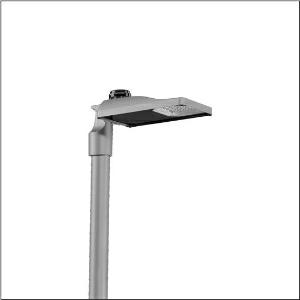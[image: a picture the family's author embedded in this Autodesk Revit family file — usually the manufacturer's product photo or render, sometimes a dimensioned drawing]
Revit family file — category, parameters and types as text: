
# Revit family: streetlight_sl_31_micro___p1_0a_5xh5a75n08da_cf7a
name_source: partatom
category: Lighting Fixtures
units: mm (PartAtom-declared; Revit-internal decimal feet)

## family parameters
Cut with Voids When Loaded = No
Host = Face
Light Source = No
Part Type = Normal
Room Calculation Point = No
Round Connector Dimension = Use Diameter
Shared = No

## types (1)
- --- (1 x LED, 3700 lm, 35.5 W, 2200K)
    Apparent Load = 36 VA
    CIE Flux Codes = 23 55 94 100 100
    Color Rendering = 70
    Color Temperature = 2200K
    Default Elevation = 1800 mm
    Description = Streetlight SL 31 micro NEMA (7pin), Desk-Remote mast luminaire for post-top, side-entry; light control with lens of PMMA; light distribution: P1.0a, direct asymmetric distribution, for standard-compliant lighting for roads and squares; LED: luminous flux: 3.700lm, light colour: 722, colour temperature: 2200K; luminous efficacy: 104,2lm/W; control: pre-setting: linear dimming characteristic, flexible luminous flux parameterisation, time-dependent luminous flux control, constant luminous flux control, intelligent temperature release in ECG and LED module, overheat protection; luminaire housing, of diecast aluminium, Siteco® metallic grey (DB 702S), corrosivity category C5 high according to DIN EN ISO 12944; cover of toughened safety glass, transparent, opened without tools; mast flange of diecast aluminium, Siteco® metallic grey (DB 702S), spigot size: 76/60mm, mast flange included unmounted; with cable H07RN-F 3x 1.5mm², cable length: 6,5m, connection cable pre-assembled; mains connection: 220..240V, AC, 50/60Hz; power consumption (at start of service life): 35,5W / (at end of service life): 37,5W / (with reduced operation 50%): 15,4W; protection rating (complete): IP66; insulation class (complete): insulation class I (protective earthing); impact resistance: IK10; certification: CE, ENEC, ENEC+, VDE, UKCA; permissible operating ambient temperature for outdoor applications: -40..+50°C; packaging unit: 1 piece

Light Distribution: P1.0a
    Height = 76 mm
    Lamp = 1 x LED
    Lamp Light Flux = 3700 lm
    Lamp Power = 35.5 W
    Lamp count = 1
    Length = 467 mm
    Luminous efficacy = 104 lm/W
    Manufacturer = Siteco
    ModVariant = No
    Model = 5XH5A75N08DA
    Number of Poles = 1
    OnlyDefault = Yes
    Power Factor = 1
    Product Name = Streetlight SL 31 micro | P1.0a
    Product group = mast luminaire | pylon top
    ProductGroupID = 6100
    Protection Class = Protection class I
    Protection Degree = IP 66
    RLX_Detail_Level = 1
    RLX_Emergency_Light_Flux = 0 lm
    RLX_Emergency_Type = 0
    RLX_Emergency_Type_DB = No
    RlxData = <blob elided: 23437 chars, md5=1adf14b5>
    Socket = socket
    Standby Power = 0 W
    System Light Flux = 3700 lm
    System Power = 36 W
    Type Comments = factory setting: luminous flux: 100 % | dim-lin: 254 | 700 mA
    Type Image = l_1300305.jpg
    URL = http://relux.com
    VarID = @adj_014949
    Voltage = 0 V
    Weight = 0.00 kg
    Width = 265 mm

## geometry (parser evidence)
native form markers: Blend x4, Sweep x9
no freeform markers — native parametric forms only
